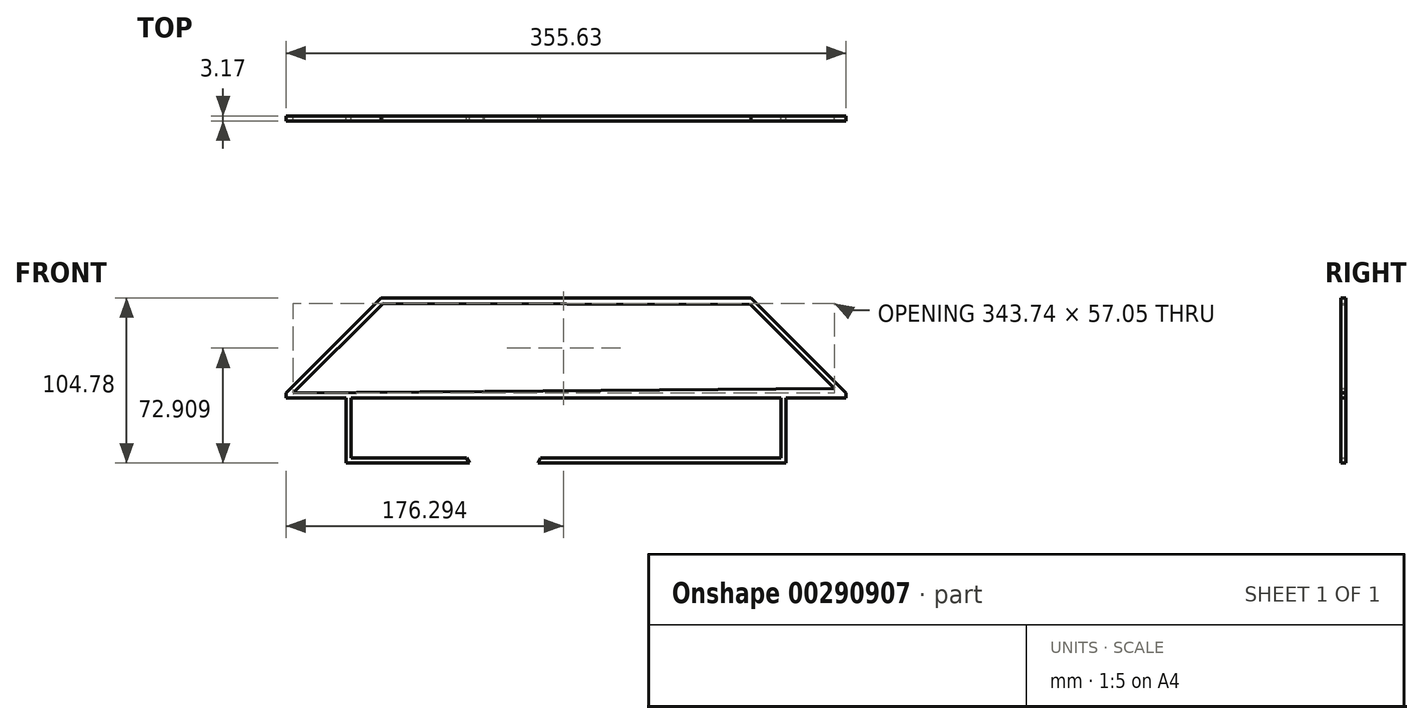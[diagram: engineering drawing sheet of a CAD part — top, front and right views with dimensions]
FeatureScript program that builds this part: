
annotation { "Feature Type Name" : "Feature", "Feature Type Description" : "" }
export const myFeature = defineFeature(function(context is Context, id is Id, definition is map)
    precondition{}
    {
        {
            var Q0;
            Q0=qCreatedBy(makeId("Front.planeOp"),FACE);
            var sketch = newSketch(context, id + "F0", { "sketchPlane" : qUnion([Q0])});
            skLineSegment(sketch, "E0.0", {"start": v(-136.53, -38.07) * mm, "end": v(136.53, -38.07) * mm});
            skLineSegment(sketch, "E1.0", {"start": v(-173.4, 3.13) * mm, "end": v(-116.35, 60.19) * mm});
            skLineSegment(sketch, "E2.MirrorCS", {"start": v(170.34, 6.2) * mm, "end": v(117.2, 59.34) * mm});
            skLineSegment(sketch, "E3.MirrorCS", {"start": v(177.8, 3.23) * mm, "end": v(117.5, 63.53) * mm});
            skLineSegment(sketch, "E4", {"start": v(-177.8, 0.03) * mm, "end": v(-139.7, 0.03) * mm});
            skLineSegment(sketch, "E5.trimOffspring", {"start": v(117.2, 59.34) * mm, "end": v(-116.35, 60.19) * mm});
            skLineSegment(sketch, "E6.trimOffspring", {"start": v(117.5, 63.53) * mm, "end": v(-117.5, 63.53) * mm});
            skLineSegment(sketch, "E7.0", {"start": v(-177.83, 3.2) * mm, "end": v(-117.5, 63.53) * mm});
            skLineSegment(sketch, "E8", {"start": v(177.8, 0.03) * mm, "end": v(177.8, 3.23) * mm});
            skLineSegment(sketch, "E9.0", {"start": v(-139.7, -41.25) * mm, "end": v(139.7, -41.25) * mm});
            skLineSegment(sketch, "E10.0", {"start": v(-136.53, 0.03) * mm, "end": v(-136.53, -38.07) * mm});
            skLineSegment(sketch, "E11.0", {"start": v(136.53, 0.03) * mm, "end": v(136.53, -38.07) * mm});
            skLineSegment(sketch, "E12.trimOffspring", {"start": v(-136.53, 0.03) * mm, "end": v(136.53, 0.03) * mm});
            skLineSegment(sketch, "E13.trimOffspring", {"start": v(139.7, 0.03) * mm, "end": v(177.8, 0.03) * mm});
            skLineSegment(sketch, "E14", {"start": v(-139.7, 0.03) * mm, "end": v(-139.7, -41.25) * mm});
            skLineSegment(sketch, "E15", {"start": v(139.7, 0.03) * mm, "end": v(139.7, -41.25) * mm});
            skLineSegment(sketch, "E16", {"start": v(-177.8, 0.03) * mm, "end": v(-177.83, 3.2) * mm});
            skLineSegment(sketch, "E17", {"start": v(0, 60.35) * mm, "end": v(0, -38.07) * mm, "construction": true});
            skLineSegment(sketch, "E18.trimOffspring", {"start": v(-173.4, 3.13) * mm, "end": v(170.34, 6.2) * mm});
            skLineSegment(sketch, "E19", {"start": v(-141.75, 3.42) * mm, "end": v(-138.94, 3.44) * mm});
            skLineSegment(sketch, "E20", {"start": v(-136.53, 0.03) * mm, "end": v(-109.02, -38.07) * mm});
            skLineSegment(sketch, "E21", {"start": v(-109.02, -38.07) * mm, "end": v(-86.27, 0.03) * mm});
            skLineSegment(sketch, "E22", {"start": v(-86.27, 0.03) * mm, "end": v(-61.47, -41.25) * mm});
            skLineSegment(sketch, "E23", {"start": v(-61.47, -41.25) * mm, "end": v(-38.2, 0.03) * mm});
            skLineSegment(sketch, "E24", {"start": v(-38.2, 0.03) * mm, "end": v(-17.75, -41.25) * mm});
            skLineSegment(sketch, "E25", {"start": v(-17.75, -41.25) * mm, "end": v(0, 0) * mm});
            skLineSegment(sketch, "E26", {"start": v(-97.65, -19.02) * mm, "end": v(-86.52, -38.07) * mm});
            skLineSegment(sketch, "E27", {"start": v(-86.52, -38.07) * mm, "end": v(-74.98, -18.75) * mm});
            skLineSegment(sketch, "E28", {"start": v(-48.79, -18.75) * mm, "end": v(-39.73, -38.07) * mm});
            skLineSegment(sketch, "E29", {"start": v(-39.73, -38.07) * mm, "end": v(-28.87, -18.8) * mm});
            skLineSegment(sketch, "E30", {"start": v(-8.87, -20.62) * mm, "end": v(0, -38.07) * mm});
            skLineSegment(sketch, "E31", {"start": v(-122.94, -18.8) * mm, "end": v(-136.53, -38.07) * mm});
            skLineSegment(sketch, "E32", {"start": v(-115.85, 60.18) * mm, "end": v(-131.53, 3.5) * mm});
            skLineSegment(sketch, "E33", {"start": v(-131.53, 3.5) * mm, "end": v(-152.28, 24.26) * mm});
            skLineSegment(sketch, "E34", {"start": v(-152.28, 24.26) * mm, "end": v(-152.1, 3.5) * mm});
            skLineSegment(sketch, "E35", {"start": v(-115.85, 60.18) * mm, "end": v(-115.36, 4.43) * mm});
            skLineSegment(sketch, "E36", {"start": v(-52, 3.5) * mm, "end": v(-52, 4.46) * mm});
            skLineSegment(sketch, "E37", {"start": v(-115.36, 4.43) * mm, "end": v(-127.82, 16.9) * mm});
            skLineSegment(sketch, "E38", {"start": v(-127.82, 16.9) * mm, "end": v(-115.36, 4.43) * mm});
            skLineSegment(sketch, "E39", {"start": v(-115.85, 60.18) * mm, "end": v(-92.56, 3.85) * mm});
            skLineSegment(sketch, "E40", {"start": v(-92.56, 3.85) * mm, "end": v(-76.57, 60.04) * mm});
            skLineSegment(sketch, "E41", {"start": v(-76.57, 60.04) * mm, "end": v(-52, 3.5) * mm});
            skLineSegment(sketch, "E42", {"start": v(-52, 3.5) * mm, "end": v(-33.77, 59.89) * mm});
            skLineSegment(sketch, "E43", {"start": v(-33.77, 59.89) * mm, "end": v(0, 4.68) * mm});
            skLineSegment(sketch, "E44", {"start": v(-115.36, 4.43) * mm, "end": v(-98.25, 17.62) * mm});
            skLineSegment(sketch, "E45", {"start": v(-152.1, 3.5) * mm, "end": v(-144.92, 16.9) * mm});
            skLineSegment(sketch, "E46", {"start": v(-76.57, 60.04) * mm, "end": v(-76.07, 4.43) * mm});
            skLineSegment(sketch, "E47", {"start": v(-33.77, 59.89) * mm, "end": v(-33.77, 4.38) * mm});
            skLineSegment(sketch, "E48", {"start": v(-33.77, 4.38) * mm, "end": v(-47.43, 17.62) * mm});
            skLineSegment(sketch, "E49", {"start": v(-47.43, 17.62) * mm, "end": v(-33.77, 4.38) * mm});
            skLineSegment(sketch, "E50", {"start": v(-33.77, 4.38) * mm, "end": v(-7.92, 17.62) * mm});
            skLineSegment(sketch, "E51", {"start": v(-76.07, 4.43) * mm, "end": v(-58.13, 17.62) * mm});
            skLineSegment(sketch, "E52", {"start": v(-58.13, 17.62) * mm, "end": v(-76.07, 4.43) * mm});
            skLineSegment(sketch, "E53", {"start": v(-76.07, 4.43) * mm, "end": v(-88.87, 16.83) * mm});
            skSolve(sketch);
        }
        {
            var Q0;
            Q0=makeQuery(id+"F0.imprint","IMPRINT",FACE,{"disambiguationData":[TD([[makeQuery(id+"F0.imprint","IMPRINT",EDGE,{"derivedFrom":sQuery(id+"F0.wireOp",EDGE,"E1.0")}),1.0]])]});
            extrude(context, id + "F1", {"entities" : qUnion([Q0]), "depth" : 3.17 * mm});
        }
    });
